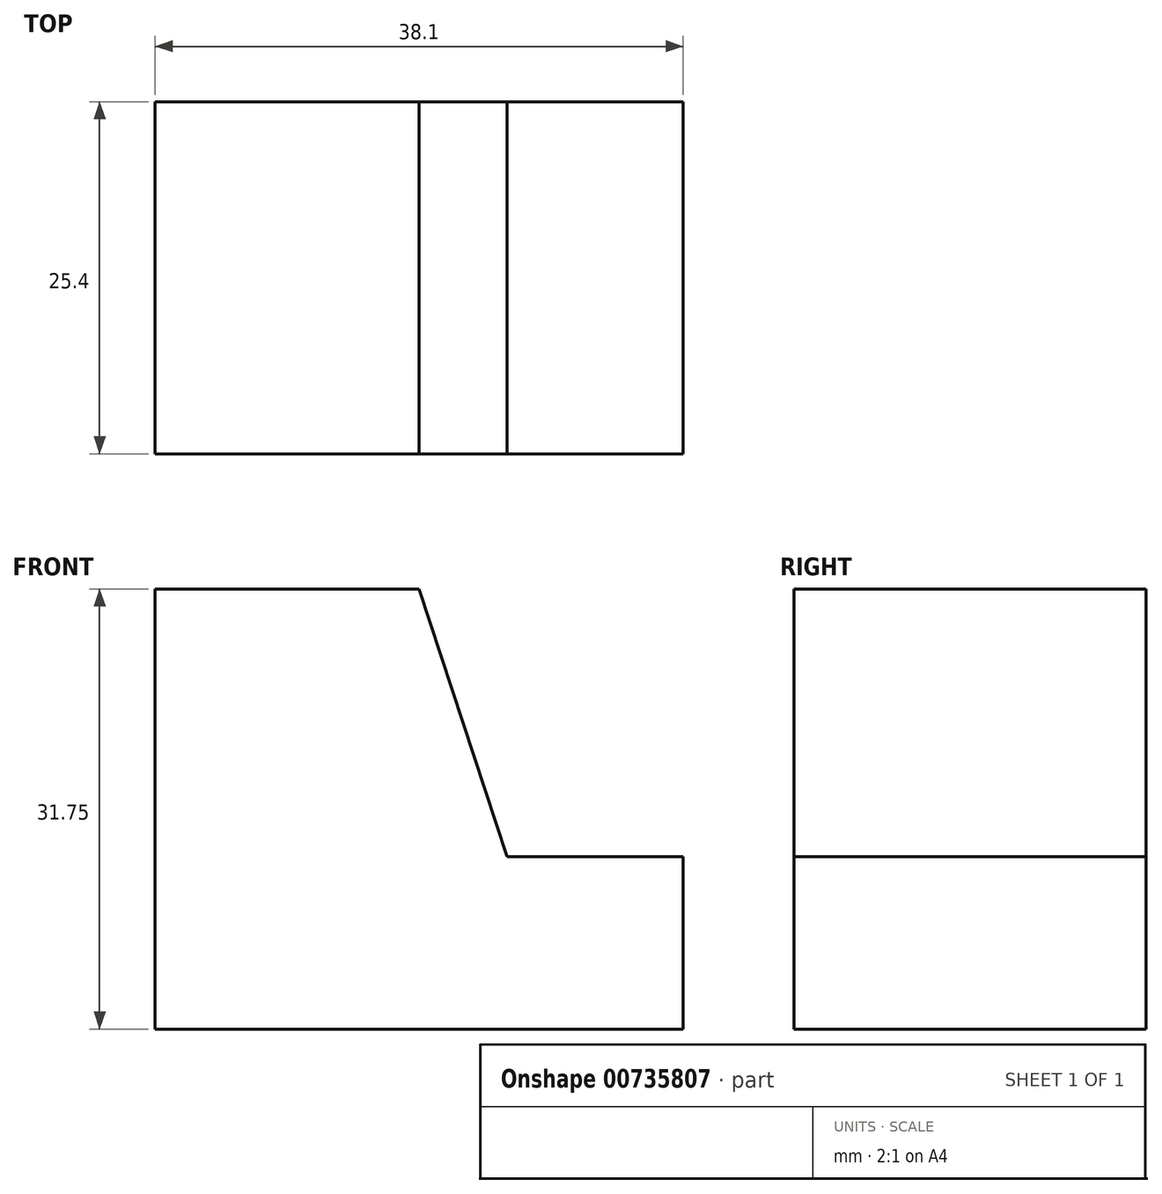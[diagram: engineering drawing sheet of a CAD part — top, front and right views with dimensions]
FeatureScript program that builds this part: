
annotation { "Feature Type Name" : "Feature", "Feature Type Description" : "" }
export const myFeature = defineFeature(function(context is Context, id is Id, definition is map)
    precondition{}
    {
        {
            var Q0;
            Q0=qCreatedBy(makeId("Front.planeOp"),FACE);
            var sketch = newSketch(context, id + "F0", { "sketchPlane" : qUnion([Q0])});
            skLineSegment(sketch, "E0", {"start": v(0, 0) * mm, "end": v(38.1, 0) * mm});
            skLineSegment(sketch, "E1", {"start": v(38.1, 0) * mm, "end": v(38.1, 31.75) * mm});
            skLineSegment(sketch, "E2", {"start": v(38.1, 31.75) * mm, "end": v(0, 31.75) * mm});
            skLineSegment(sketch, "E3", {"start": v(0, 31.75) * mm, "end": v(0, 0) * mm});
            skLineSegment(sketch, "E4", {"start": v(19.05, 31.75) * mm, "end": v(25.4, 12.45) * mm});
            skLineSegment(sketch, "E5", {"start": v(25.4, 12.45) * mm, "end": v(38.1, 12.45) * mm});
            skSolve(sketch);
        }
        {
            var Q0;
            {var subQ4=sQuery(id+"F0.wireOp",EDGE,"E0");Q0=makeQuery(id+"F0.imprint","IMPRINT",FACE,{"disambiguationData":[TD([[makeQuery(id+"F0.imprint","IMPRINT",EDGE,{"derivedFrom":subQ4}),1.0]])]});}
            extrude(context, id + "F1", {"entities" : qUnion([Q0]), "depth" : 25.4 * mm, "offsetDistance" : 25.4 * mm});
        }
    });
